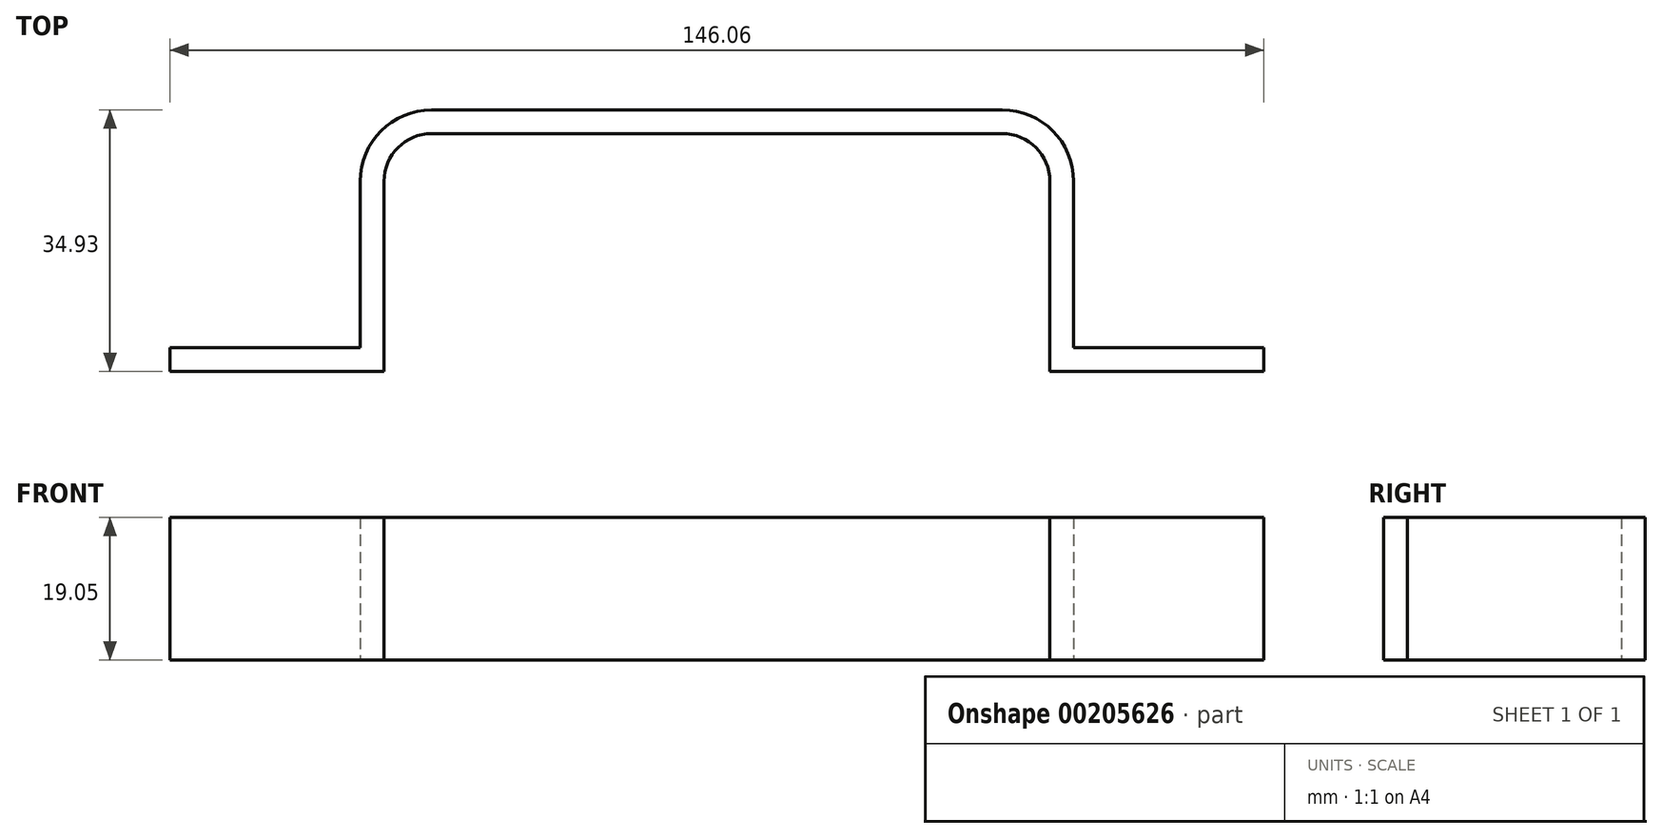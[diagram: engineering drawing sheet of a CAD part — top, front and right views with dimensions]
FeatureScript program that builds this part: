
annotation { "Feature Type Name" : "Feature", "Feature Type Description" : "" }
export const myFeature = defineFeature(function(context is Context, id is Id, definition is map)
    precondition{}
    {
        {
            var Q0;
            Q0=qCreatedBy(makeId("Top.planeOp"),FACE);
            var sketch = newSketch(context, id + "F0", { "sketchPlane" : qUnion([Q0])});
            skLineSegment(sketch, "E0.bottom", {"start": v(-38.1, 1.59) * mm, "end": v(38.1, 1.59) * mm});
            skLineSegment(sketch, "E0.top", {"start": v(-38.1, -1.59) * mm, "end": v(38.1, -1.59) * mm});
            skLineSegment(sketch, "E0.left", {"start": v(-38.1, 1.59) * mm, "end": v(-38.1, -1.59) * mm});
            skLineSegment(sketch, "E0.right", {"start": v(38.1, 1.59) * mm, "end": v(38.1, -1.59) * mm});
            skPoint(sketch, "E1", {"position": v(0, 1.59) * mm});
            skPoint(sketch, "E2", {"position": v(0, -1.59) * mm});
            skLineSegment(sketch, "E3", {"start": v(0, 1.59) * mm, "end": v(0, -1.59) * mm});
            skPoint(sketch, "E4", {"position": v(0, 0) * mm});
            skLineSegment(sketch, "E5.bottom", {"start": v(-47.63, -7.94) * mm, "end": v(-44.45, -7.94) * mm});
            skLineSegment(sketch, "E5.top", {"start": v(-47.63, -33.34) * mm, "end": v(-44.45, -33.34) * mm});
            skLineSegment(sketch, "E5.left", {"start": v(-47.62, -7.94) * mm, "end": v(-47.62, -33.34) * mm});
            skLineSegment(sketch, "E5.right", {"start": v(-44.45, -7.94) * mm, "end": v(-44.45, -33.34) * mm});
            skLineSegment(sketch, "E6.bottom", {"start": v(-73.03, -30.16) * mm, "end": v(-47.63, -30.16) * mm});
            skLineSegment(sketch, "E6.top", {"start": v(-73.03, -33.34) * mm, "end": v(-47.63, -33.34) * mm});
            skLineSegment(sketch, "E6.left", {"start": v(-73.03, -30.16) * mm, "end": v(-73.03, -33.34) * mm});
            skLineSegment(sketch, "E6.right", {"start": v(-47.63, -30.16) * mm, "end": v(-47.63, -33.34) * mm});
            skCircle(sketch, "E7", {"center": v(-38.1, -7.94) * mm, "radius": 6.35 * mm});
            skLineSegment(sketch, "E8", {"start": v(-44.45, -7.94) * mm, "end": v(-31.75, -7.94) * mm});
            skLineSegment(sketch, "E9", {"start": v(-38.1, -1.59) * mm, "end": v(-38.1, -14.29) * mm});
            skCircle(sketch, "E10", {"center": v(-38.1, -7.94) * mm, "radius": 9.53 * mm});
            skCircle(sketch, "E11", {"center": v(38.1, -7.94) * mm, "radius": 6.35 * mm});
            skLineSegment(sketch, "E12", {"start": v(31.75, -7.94) * mm, "end": v(44.45, -7.94) * mm});
            skLineSegment(sketch, "E13", {"start": v(38.1, -1.59) * mm, "end": v(38.1, -14.29) * mm});
            skCircle(sketch, "E14", {"center": v(38.1, -7.94) * mm, "radius": 9.53 * mm});
            skLineSegment(sketch, "E15.bottom", {"start": v(44.45, -7.94) * mm, "end": v(47.63, -7.94) * mm});
            skLineSegment(sketch, "E15.top", {"start": v(44.45, -33.34) * mm, "end": v(47.63, -33.34) * mm});
            skLineSegment(sketch, "E15.left", {"start": v(44.45, -7.94) * mm, "end": v(44.45, -33.34) * mm});
            skLineSegment(sketch, "E15.right", {"start": v(47.63, -7.94) * mm, "end": v(47.63, -33.34) * mm});
            skLineSegment(sketch, "E16.bottom", {"start": v(47.63, -33.34) * mm, "end": v(73.03, -33.34) * mm});
            skLineSegment(sketch, "E16.top", {"start": v(47.63, -30.16) * mm, "end": v(73.03, -30.16) * mm});
            skLineSegment(sketch, "E16.left", {"start": v(47.63, -33.34) * mm, "end": v(47.63, -30.16) * mm});
            skLineSegment(sketch, "E16.right", {"start": v(73.03, -33.34) * mm, "end": v(73.03, -30.16) * mm});
            skSolve(sketch);
        }
        {
            var Q0;
            {var subQ0=sQuery(id+"F0.wireOp",EDGE,"E0.left");Q0=makeQuery(id+"F0.imprint","IMPRINT",FACE,{"disambiguationData":[TD([[makeQuery(id+"F0.imprint","IMPRINT",EDGE,{"derivedFrom":subQ0}),-1.0]])]});}
            var Q1;
            {var subQ0=sQuery(id+"F0.wireOp",EDGE,"E5.bottom");Q1=makeQuery(id+"F0.imprint","IMPRINT",FACE,{"disambiguationData":[TD([[makeQuery(id+"F0.imprint","IMPRINT",EDGE,{"derivedFrom":subQ0}),-1.0]])]});}
            var Q2;
            {var subQ1=sQuery(id+"F0.wireOp",EDGE,"E5.top");Q2=makeQuery(id+"F0.imprint","IMPRINT",FACE,{"disambiguationData":[TD([[makeQuery(id+"F0.imprint","IMPRINT",EDGE,{"derivedFrom":subQ1}),1.0]])]});}
            var Q3;
            Q3=makeQuery(id+"F0.imprint","IMPRINT",FACE,{"disambiguationData":[TD([[makeQuery(id+"F0.imprint","IMPRINT",EDGE,{"derivedFrom":sQuery(id+"F0.wireOp",EDGE,"E6.bottom")}),-1.0]])]});
            var Q4;
            {var subQ0=sQuery(id+"F0.wireOp",EDGE,"E0.left");Q4=makeQuery(id+"F0.imprint","IMPRINT",FACE,{"disambiguationData":[TD([[makeQuery(id+"F0.imprint","IMPRINT",EDGE,{"derivedFrom":subQ0}),1.0]])]});}
            var Q5;
            {var subQ3=sQuery(id+"F0.wireOp",EDGE,"E3");Q5=makeQuery(id+"F0.imprint","IMPRINT",FACE,{"disambiguationData":[TD([[makeQuery(id+"F0.imprint","IMPRINT",EDGE,{"derivedFrom":subQ3}),-1.0]])]});}
            var Q6;
            {var subQ3=sQuery(id+"F0.wireOp",EDGE,"E3");Q6=makeQuery(id+"F0.imprint","IMPRINT",FACE,{"disambiguationData":[TD([[makeQuery(id+"F0.imprint","IMPRINT",EDGE,{"derivedFrom":subQ3}),1.0]])]});}
            var Q7;
            {var subQ0=sQuery(id+"F0.wireOp",EDGE,"E0.right");Q7=makeQuery(id+"F0.imprint","IMPRINT",FACE,{"disambiguationData":[TD([[makeQuery(id+"F0.imprint","IMPRINT",EDGE,{"derivedFrom":subQ0}),-1.0]])]});}
            var Q8;
            {var subQ0=sQuery(id+"F0.wireOp",EDGE,"E0.right");Q8=makeQuery(id+"F0.imprint","IMPRINT",FACE,{"disambiguationData":[TD([[makeQuery(id+"F0.imprint","IMPRINT",EDGE,{"derivedFrom":subQ0}),1.0]])]});}
            var Q9;
            {var subQ0=sQuery(id+"F0.wireOp",EDGE,"E15.bottom");Q9=makeQuery(id+"F0.imprint","IMPRINT",FACE,{"disambiguationData":[TD([[makeQuery(id+"F0.imprint","IMPRINT",EDGE,{"derivedFrom":subQ0}),-1.0]])]});}
            var Q10;
            {var subQ2=sQuery(id+"F0.wireOp",EDGE,"E15.top");Q10=makeQuery(id+"F0.imprint","IMPRINT",FACE,{"disambiguationData":[TD([[makeQuery(id+"F0.imprint","IMPRINT",EDGE,{"derivedFrom":subQ2}),1.0]])]});}
            var Q11;
            Q11=makeQuery(id+"F0.imprint","IMPRINT",FACE,{"disambiguationData":[TD([[makeQuery(id+"F0.imprint","IMPRINT",EDGE,{"derivedFrom":sQuery(id+"F0.wireOp",EDGE,"E16.bottom")}),1.0]])]});
            extrude(context, id + "F1", {"entities" : qUnion([Q0, Q1, Q2, Q3, Q4, Q5, Q6, Q7, Q8, Q9, Q10, Q11]), "depth" : 19.05 * mm});
        }
    });
